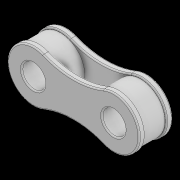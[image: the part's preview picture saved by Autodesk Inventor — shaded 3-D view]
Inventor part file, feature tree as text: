
AUTODESK INVENTOR PART (.ipt)
format: ipt  version: 2021 (Build 250183000, 183)  size: 219,648 bytes
history: native  units: in
note: dims shown in document units (in); Inventor stores cm internally (conversion verified against a paired STEP export)
features: extrude x2, sketch x2, plane x1, mirror x1, fillet x1
ambient origin geometry x8: Origin, YZ Plane, XZ Plane, XY Plane, X Axis, Y Axis, Z Axis, Center Point
bodies: Solid1 (feature_tree)
feature tree (7):
  plane  "Work Plane1"
  extrude  "Extrusion1"  Depth=0.1441in
  mirror  "Mirror1"
  extrude  "Extrusion2"  Depth=0.0079in
  fillet  "Fillet1"  Radius=0.5in
  sketch  "Sketch1"  dims[d1=0.3051in d2=0.1441in]
  sketch  "Sketch2"  dims[d0=0.065in d3=0.3228in d4=0.5in d5=0.4921in d6=0.1441in d7=0.0394in d8=0.0in d9=0.3051in d10=0.1299in d11=0.0in d12=0.0079in]
